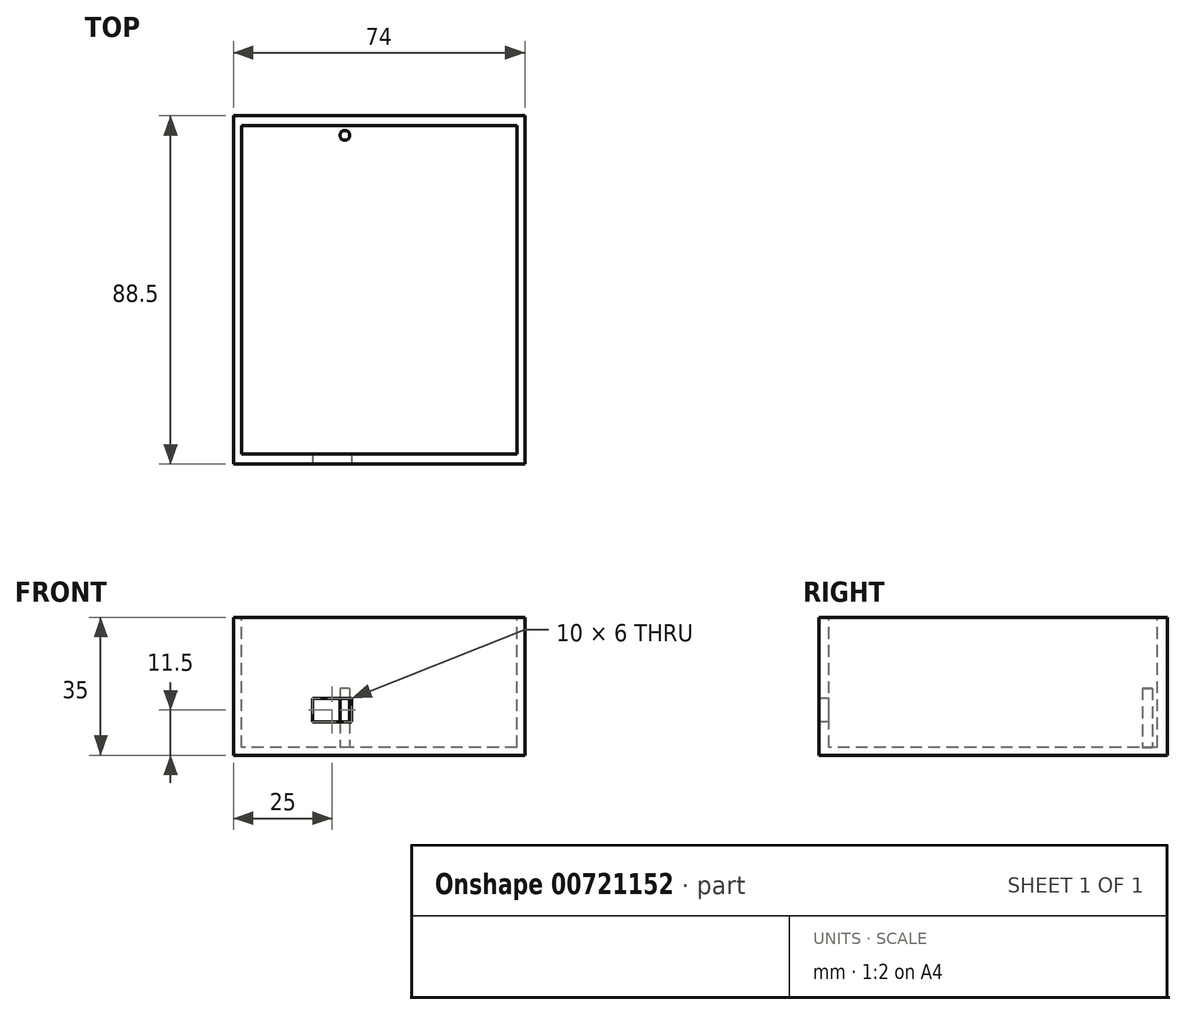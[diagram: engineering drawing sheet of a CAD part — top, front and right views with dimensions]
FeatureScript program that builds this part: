
annotation { "Feature Type Name" : "Feature", "Feature Type Description" : "" }
export const myFeature = defineFeature(function(context is Context, id is Id, definition is map)
    precondition{}
    {
        {
            var Q0;
            Q0=qCreatedBy(makeId("Top.planeOp"),FACE);
            var sketch = newSketch(context, id + "F0", { "sketchPlane" : qUnion([Q0])});
            skLineSegment(sketch, "E0.bottom", {"start": v(37, 44.25) * mm, "end": v(-37, 44.25) * mm});
            skLineSegment(sketch, "E0.top", {"start": v(37, -44.25) * mm, "end": v(-37, -44.25) * mm});
            skLineSegment(sketch, "E0.left", {"start": v(37, 44.25) * mm, "end": v(37, -44.25) * mm});
            skLineSegment(sketch, "E0.right", {"start": v(-37, 44.25) * mm, "end": v(-37, -44.25) * mm});
            skPoint(sketch, "E0.middle", {"position": v(0, 0) * mm});
            skSolve(sketch);
        }
        {
            var Q0;
            Q0=qSketchRegion(id+"F0",true);
            extrude(context, id + "F1", {"entities" : qUnion([Q0]), "depth" : 34 * mm, "offsetDistance" : 25 * mm});
        }
        {
            var Q0;
            Q0=makeQuery(id+"F1.opExtrude","CAP_FACE",FACE,{"disambiguationData":[OSD([sQuery(id+"F0.wireOp",EDGE,"E0.bottom"),sQuery(id+"F0.wireOp",EDGE,"E0.top"),sQuery(id+"F0.wireOp",EDGE,"E0.left"),sQuery(id+"F0.wireOp",EDGE,"E0.right")])],"isStart":false});
            var sketch = newSketch(context, id + "F2", { "sketchPlane" : qUnion([Q0])});
            skLineSegment(sketch, "E1.bottom", {"start": v(35, 41.75) * mm, "end": v(-35, 41.75) * mm});
            skLineSegment(sketch, "E1.top", {"start": v(35, -41.75) * mm, "end": v(-35, -41.75) * mm});
            skLineSegment(sketch, "E1.left", {"start": v(35, 41.75) * mm, "end": v(35, -41.75) * mm});
            skLineSegment(sketch, "E1.right", {"start": v(-35, 41.75) * mm, "end": v(-35, -41.75) * mm});
            skPoint(sketch, "E1.middle", {"position": v(0, 0) * mm});
            skSolve(sketch);
        }
        {
            var Q0;
            Q0=qSketchRegion(id+"F2",true);
            extrude(context, id + "F3", {"entities" : qUnion([Q0]), "operationType" : NewBodyOperationType.REMOVE, "oppositeDirection" : true, "depth" : 33 * mm, "offsetDistance" : 25 * mm});
        }
        {
            var Q0;
            Q0=makeQuery(id+"F3.boolean.opBoolean","COPY",FACE,{"derivedFrom":makeQuery(id+"F3.opExtrude","CAP_FACE",FACE,{"disambiguationData":[OSD([sQuery(id+"F2.wireOp",EDGE,"E1.bottom"),sQuery(id+"F2.wireOp",EDGE,"E1.top"),sQuery(id+"F2.wireOp",EDGE,"E1.left"),sQuery(id+"F2.wireOp",EDGE,"E1.right")])],"isStart":false})});
            var sketch = newSketch(context, id + "F4", { "sketchPlane" : qUnion([Q0])});
            skLineSegment(sketch, "E2.bottom", {"start": v(-35, 41.75) * mm, "end": v(-8.75, 41.75) * mm});
            skLineSegment(sketch, "E2.top", {"start": v(-35, 39.25) * mm, "end": v(-8.75, 39.25) * mm});
            skLineSegment(sketch, "E2.left", {"start": v(-35, 41.75) * mm, "end": v(-35, 39.25) * mm});
            skLineSegment(sketch, "E2.right", {"start": v(-8.75, 41.75) * mm, "end": v(-8.75, 39.25) * mm});
            skCircle(sketch, "E3", {"center": v(-8.75, 39.25) * mm, "radius": 1.25 * mm});
            skSolve(sketch);
        }
        {
            var Q0;
            {var subQ0=sQuery(id+"F4.wireOp",EDGE,"E2.right");var subQ1=sQuery(id+"F4.wireOp",EDGE,"E2.top");var subQ2=makeQuery(id+"F4.imprint","INTERSECT",VERTEX,{"derivedFrom":[subQ1,subQ0]});Q0=makeQuery(id+"F4.imprint","IMPRINT",FACE,{"disambiguationData":[TD([[makeQuery(id+"F4.imprint","IMPRINT",EDGE,{"disambiguationData":[TD([[subQ2,1.0]])],"derivedFrom":subQ1}),-1.0]])]});}
            var Q1;
            {var subQ0=sQuery(id+"F4.wireOp",EDGE,"E2.right");var subQ1=sQuery(id+"F4.wireOp",EDGE,"E2.top");var subQ2=makeQuery(id+"F4.imprint","INTERSECT",VERTEX,{"derivedFrom":[subQ1,subQ0]});Q1=makeQuery(id+"F4.imprint","IMPRINT",FACE,{"disambiguationData":[TD([[makeQuery(id+"F4.imprint","IMPRINT",EDGE,{"disambiguationData":[TD([[subQ2,1.0]])],"derivedFrom":subQ1}),1.0]])]});}
            extrude(context, id + "F5", {"entities" : qUnion([Q0, Q1]), "operationType" : NewBodyOperationType.ADD, "depth" : 15 * mm, "offsetDistance" : 25 * mm});
        }
        {
            var Q0;
            Q0=qSketchRegion(id+"F0",true);
            var Q1;
            Q1=makeQuery(id+"F0.imprint","IMPRINT",FACE,{"disambiguationData":[TD([[makeQuery(id+"F0.imprint","IMPRINT",EDGE,{"derivedFrom":sQuery(id+"F0.wireOp",EDGE,"E0.bottom")}),1.0]])]});
            extrude(context, id + "F6", {"entities" : qUnion([Q0, Q1]), "operationType" : NewBodyOperationType.ADD, "oppositeDirection" : true, "depth" : 1 * mm, "offsetDistance" : 25 * mm});
        }
        {
            var Q0;
            {var subQ0=sQuery(id+"F0.wireOp",EDGE,"E0.top");Q0=makeQuery(id+"F6.boolean.opBoolean","MERGE",FACE,{"derivedFrom":[makeQuery(id+"F1.opExtrude","SWEPT_FACE",FACE,{"disambiguationData":[OSD([subQ0])]}),makeQuery(id+"F6.opExtrude","SWEPT_FACE",FACE,{"disambiguationData":[OSD([subQ0])]})]});}
            var sketch = newSketch(context, id + "F7", { "sketchPlane" : qUnion([Q0])});
            skLineSegment(sketch, "E4", {"start": v(0, -1) * mm, "end": v(0, 7.5) * mm});
            skLineSegment(sketch, "E5", {"start": v(-37, 7.5) * mm, "end": v(-7, 7.5) * mm});
            skLineSegment(sketch, "E6", {"start": v(-7, 7.5) * mm, "end": v(-7, 13.5) * mm});
            skLineSegment(sketch, "E7", {"start": v(-7, 13.5) * mm, "end": v(-17, 13.5) * mm});
            skLineSegment(sketch, "E8", {"start": v(-17, 13.5) * mm, "end": v(-17, 7.5) * mm});
            skSolve(sketch);
        }
        {
            var Q0;
            {var subQ0=sQuery(id+"F7.wireOp",EDGE,"E6");Q0=makeQuery(id+"F7.imprint","IMPRINT",FACE,{"disambiguationData":[TD([[makeQuery(id+"F7.imprint","IMPRINT",EDGE,{"derivedFrom":subQ0}),1.0]])]});}
            extrude(context, id + "F8", {"entities" : qUnion([Q0]), "operationType" : NewBodyOperationType.REMOVE, "oppositeDirection" : true, "depth" : 25 * mm, "offsetDistance" : 25 * mm});
        }
    });
